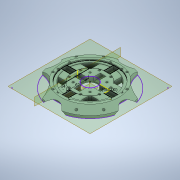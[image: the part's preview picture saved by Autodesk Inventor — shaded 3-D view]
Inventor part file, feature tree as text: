
AUTODESK INVENTOR PART (.ipt)
format: ipt  version: 2020 (Build 240168000, 168)  size: 613,888 bytes
history: native  units: mm
features: extrude x12, sketch x11, projected_geometry x8, other x6, pattern_circular x3, revolve x1, hole x1
ambient origin geometry x8: Origin, YZ Plane, XZ Plane, XY Plane, X Axis, Y Axis, Z Axis, Center Point
bodies: Body1 (feature_tree)
feature tree (42):
  other  "Твердое тело1"
  sketch  "Эскиз1"
  sketch  "Эскиз2"
  sketch  "Эскиз3"
  other  "РабОсь1"
  revolve  "Вращение1"
  hole  "Отверстие1"  [1 undecoded]
  other  "РабПлоскость1"
  other  "РабПлоскость2"
  extrude  "Выдавливание2"  Depth=44.0mm
  pattern_circular  "Круговой массив1"  Count=4 Angle=360.0deg
  other  "РабПлоскость3"
  extrude  "Выдавливание6"  Depth=7.0mm
  extrude  "Выдавливание7"  Depth=13.0mm
  pattern_circular  "Круговой массив2"  Angle=90.0deg  [1 undecoded]
  extrude  "Выдавливание8"  [1 undecoded]
  pattern_circular  "Круговой массив3"  [2 undecoded]
  extrude  "Выдавливание9"  Depth=6.0mm
  extrude  "Выдавливание10"  Depth=6.0mm
  other  "РабПлоскость4"
  extrude  "Выдавливание11"  Depth=6.0mm
  extrude  "Выдавливание1"  Depth=6.0mm
  extrude  "Выдавливание12"  Depth=6.0mm
  extrude  "Выдавливание13"  Depth=6.0mm
  extrude  "Выдавливание14"  Depth=6.0mm
  sketch  "Эскиз14"
  extrude  "Выдавливание15"  Depth=6.0mm
  sketch  "Эскиз5"
  sketch  "Эскиз9"
  sketch  "Эскиз10"
  sketch  "Эскиз11"
  sketch  "Эскиз12"
  sketch  "Эскиз13"
  projected_geometry  "Спроецированная петля1"
  projected_geometry  "Спроецированная петля2"
  projected_geometry  "Спроецированная петля3"
  projected_geometry  "Спроецированная петля4"
  projected_geometry  "Спроецированная петля5"
  projected_geometry  "Спроецированная петля6"
  projected_geometry  "Спроецированная петля7"
  projected_geometry  "Спроецированная петля8"
  sketch  "Эскиз15"
note: 5 required parameter values undecoded (feature->parameter linkage not recoverable at this tier; creation-order binding heuristic only, values carry confidence <= 0.55)
